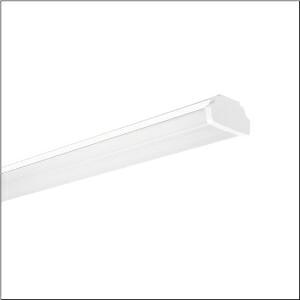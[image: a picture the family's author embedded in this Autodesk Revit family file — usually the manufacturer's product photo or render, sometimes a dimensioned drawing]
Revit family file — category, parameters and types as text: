
# Revit family: modario_r__31_gen_2_53bm812cv49xc2_cf0d
name_source: partatom
category: Lighting Fixtures
units: mm (PartAtom-declared; Revit-internal decimal feet)

## family parameters
Cut with Voids When Loaded = No
Host = Face
Light Source = No
Part Type = Normal
Room Calculation Point = No
Round Connector Dimension = Use Diameter
Shared = No

## types (1)
- --- (1 x LED, 9240 lm, 49.9 W, 4000K)
    Apparent Load = 50 VA
    CIE Flux Codes = 47 80 95 93 100
    Color Rendering = 80
    Color Temperature = 4000K
    Default Elevation = 1800 mm
    Description = Modario® 31 Gen.2, luminaire insert, of sheet steel, coil coated, white, length: 1.495mm, width: 81mm, height: 82mm, 5x system unit, system units: 299mm, LED rated luminous flux: 9.240lm, light colour: 840, control gear: ON/OFF Multilumen, CLOi, with plug, 3-pole, with phase selection, mains connection: 220..240V, AC, 50/60Hz, start of lifetime: 50W, end of service life: 61W, through-wiring accessed according to module size, primary optical cover: cover, of PMMA, light emission: direct distribution, primary light characteristic: symmetric, protection rating (complete): IP20, protection rating (LED compartment): IP50, insulation class (complete): insulation class I (protective earthing), certification: CE, ENEC, VDE, UKCA, impact resistance: IK03, permissible ambient temperature for indoor applications: -35..+40°C, corresponds to IFS (International Featured Standards) requirements for safety and quality in the food industry, reducing of maximum allowable ambient temperature of 5°C with ceiling mounting, IP40 when using the optional accessory 5TP9018, packaging unit: 1 piece
    Height = 92 mm
    Lamp = 1 x LED
    Lamp Light Flux = 9240 lm
    Lamp Power = 49.9 W
    Lamp count = 1
    Length = 1495 mm
    Luminous efficacy = 185 lm/W
    Manufacturer = Siteco
    ModVariant = No
    Model = 53BM812CV49XC2
    Mounting Place = Ceiling
    Mounting Type = Pendant
    Number of Poles = 1
    OnlyDefault = Yes
    Power Factor = 1
    Product Name = Modario® 31 Gen.2
    Product group = luminaire insert
    ProductGroupID = 901
    Protection Class = Protection class I
    Protection Degree = IP 20
    RLX_Detail_Level = 1
    RLX_Emergency_Light_Flux = 0 lm
    RLX_Emergency_Type = 0
    RLX_Emergency_Type_DB = No
    RlxData = <blob elided: 40085 chars, md5=8d151dd8>
    Socket = socket
    Standby Power = 0 W
    System Light Flux = 9240 lm
    System Power = 50 W
    Type Comments = factory setting: luminous flux: 100 % | (A | C | E) | 116 mA
    Type Image = l_1319597.jpg
    URL = http://relux.com
    VarID = @adj_010649
    Voltage = 0 V
    Weight = 0.00 kg
    Width = 81 mm

## geometry (parser evidence)
native form markers: Blend x4, Sweep x11
no freeform markers — native parametric forms only
